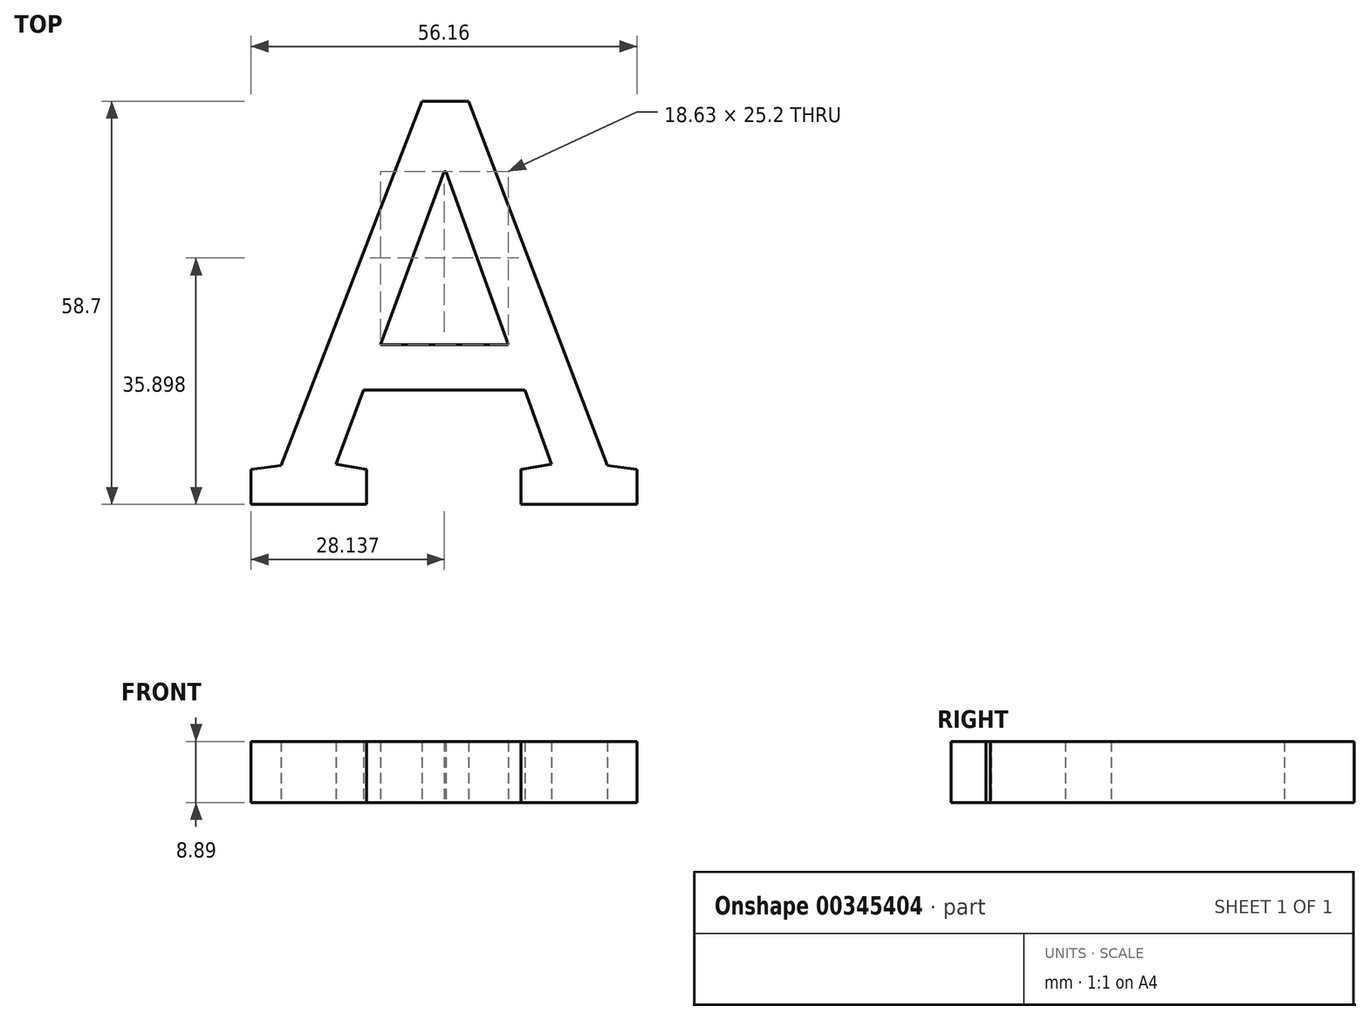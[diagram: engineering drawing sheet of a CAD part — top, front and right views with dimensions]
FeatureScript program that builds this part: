
annotation { "Feature Type Name" : "Feature", "Feature Type Description" : "" }
export const myFeature = defineFeature(function(context is Context, id is Id, definition is map)
    precondition{}
    {
        {
            var Q0;
            Q0=qCreatedBy(makeId("Top.planeOp"),FACE);
            var sketch = newSketch(context, id + "F0", { "sketchPlane" : qUnion([Q0])});
            skText(sketch, "E0", { "text": "A", "fontName": "RobotoSlab-Regular.ttf"});
            const initialGuessF0  = {"E0": [0, 0, 1, 0, 0.05945]};
            skSetInitialGuess(sketch, initialGuessF0);
            skSolve(sketch);
        }
        {
            var Q0;
            Q0 = qSketchRegion(id + "F0", true);
            extrude(context, id + "F1", {"entities" : qUnion([Q0]), "depth" : 8.9 * mm});
        }
    });
